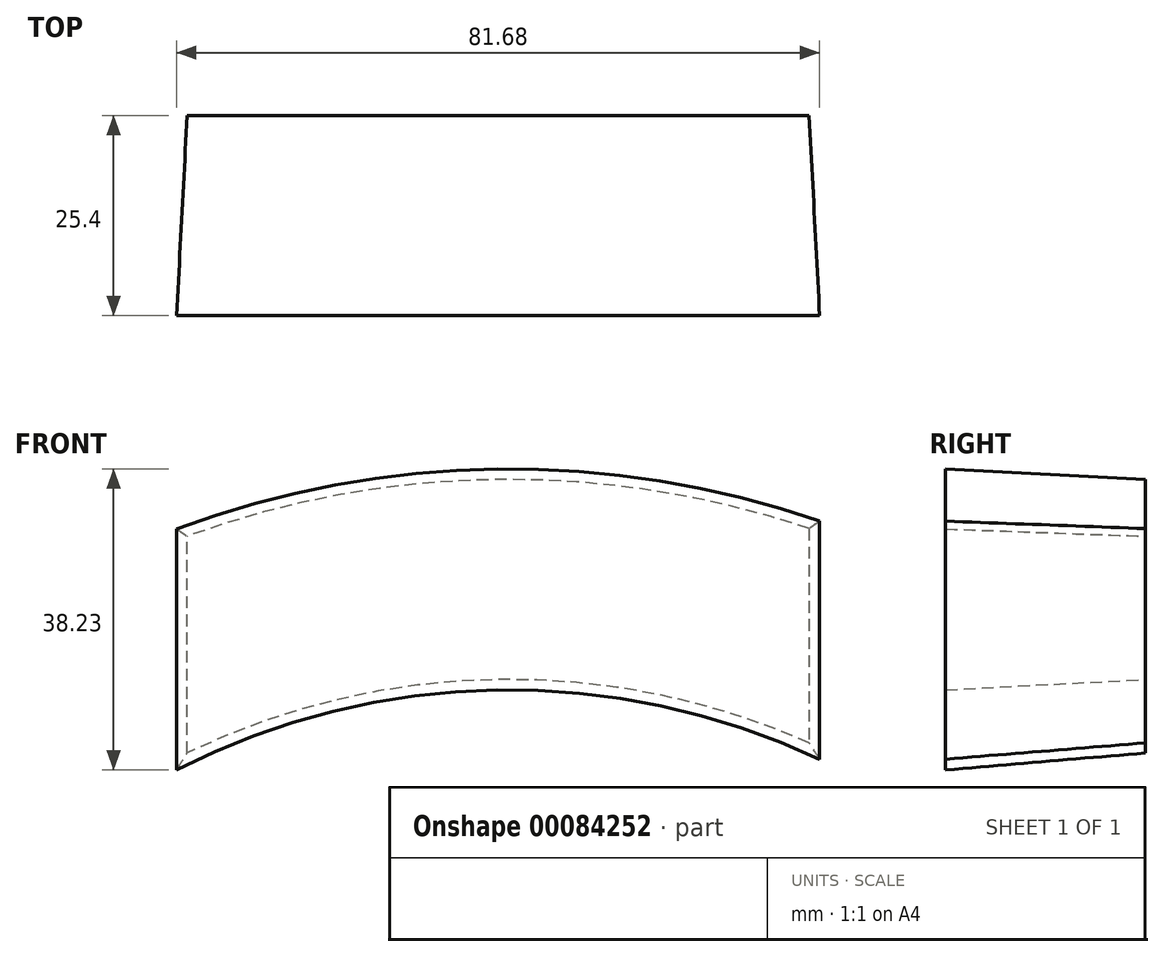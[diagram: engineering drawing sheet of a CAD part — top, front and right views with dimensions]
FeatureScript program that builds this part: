
annotation { "Feature Type Name" : "Feature", "Feature Type Description" : "" }
export const myFeature = defineFeature(function(context is Context, id is Id, definition is map)
    precondition{}
    {
        {
            var Q0;
            Q0=qCreatedBy(makeId("Front.planeOp"),FACE);
            var sketch = newSketch(context, id + "F0", { "sketchPlane" : qUnion([Q0])});
            skLineSegment(sketch, "E0.left", {"start": v(-60.33, 51.46) * mm, "end": v(-60.33, 23.92) * mm});
            skLineSegment(sketch, "E0.right", {"start": v(18.69, 52.43) * mm, "end": v(18.69, 25.2) * mm});
            skArc(sketch, "E1", {"start": v(18.69, 25.2) * mm, "mid": v(-20.96, 33.26) * mm, "end": v(-60.33, 23.92) * mm});
            skArc(sketch, "E2.0", {"start": v(18.69, 52.43) * mm, "mid": v(-20.9, 58.66) * mm, "end": v(-60.33, 51.46) * mm});
            skSolve(sketch);
        }
        {
            var Q0;
            Q0=makeQuery(id+"F0.imprint","IMPRINT",FACE,{"disambiguationData":[TD([[makeQuery(id+"F0.imprint","IMPRINT",EDGE,{"derivedFrom":sQuery(id+"F0.wireOp",EDGE,"E0.left")}),1.0]])]});
            extrude(context, id + "F1", {"entities" : qUnion([Q0]), "depth" : 25.4 * mm, "hasDraft" : true, "draftAngle" : 3 * degree});
        }
    });
